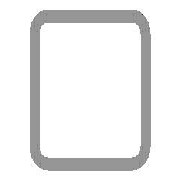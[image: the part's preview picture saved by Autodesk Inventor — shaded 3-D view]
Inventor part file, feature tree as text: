
AUTODESK INVENTOR PART (.ipt)
format: ipt  version: 2025 (Build 290162010, 162A)  size: 134,656 bytes
history: native  units: mm (DEFAULTED — no unit token found)
features: other x4, sketch x1, plane x1
ambient origin geometry x8: Origin, YZ Plane, XZ Plane, XY Plane, X Axis, Y Axis, Z Axis, Center Point
bodies: Solid1 (feature_tree), Body (feature_tree)
feature tree (6):
  parser-record x1  (decoder bookkeeping rows leaked as tree rows — omitted from the tree; the rows remain in map.json)
  other  "Driven Length"
  other  "Start plane"
  other  "End plane"
  sketch  "Sketch3"  dims[d3=2290.0mm d4=0.0mm d7=6.0mm d9=80.0mm d11=80.0mm d12=3.0mm d13=80.0mm d14=2370.0mm d15=40.0mm d16=40.0mm d17=90.0deg d18=2290.0mm]
  plane  "Work Plane3"
